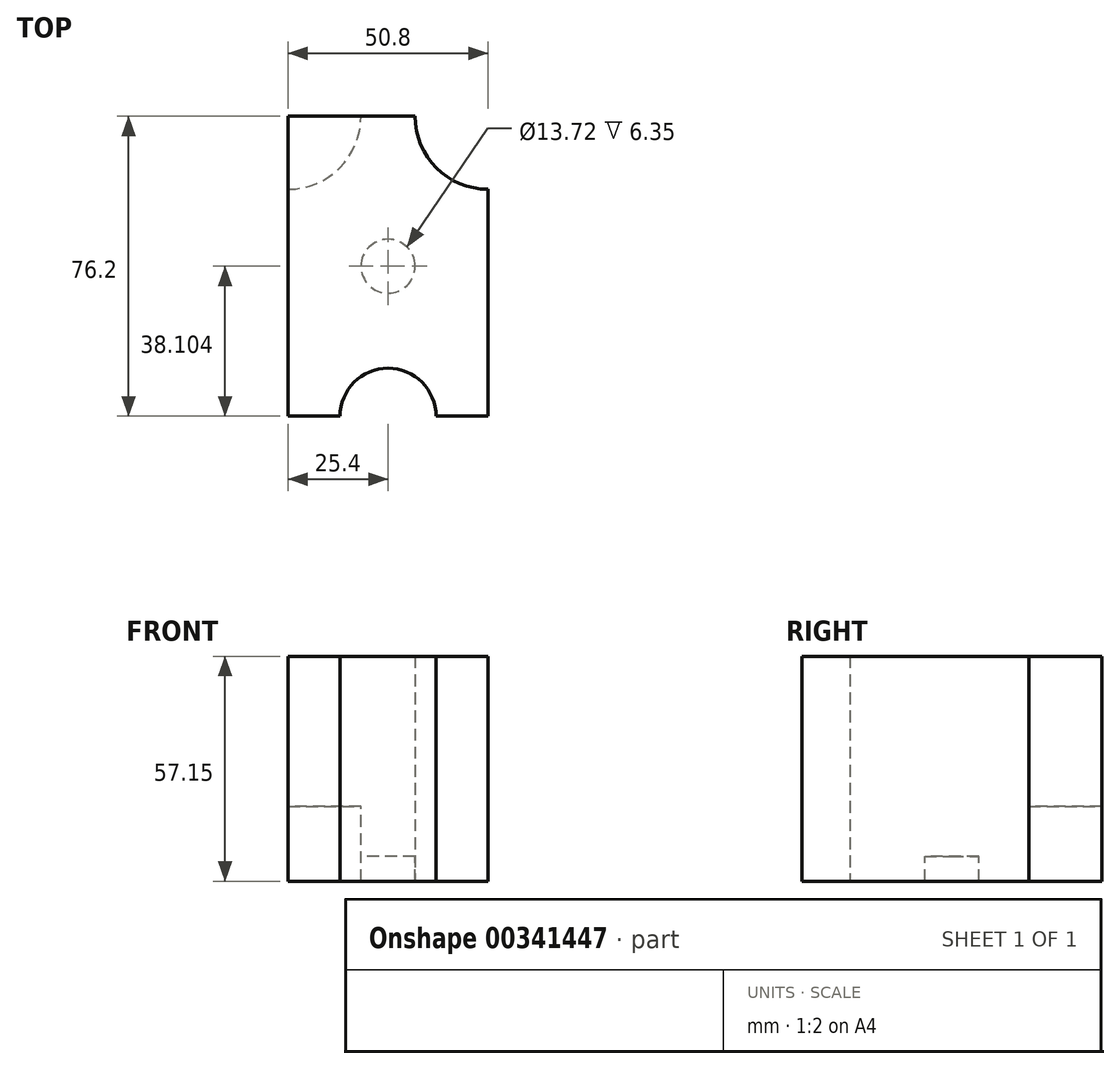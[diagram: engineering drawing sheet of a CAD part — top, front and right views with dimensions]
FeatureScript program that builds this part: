
annotation { "Feature Type Name" : "Feature", "Feature Type Description" : "" }
export const myFeature = defineFeature(function(context is Context, id is Id, definition is map)
    precondition{}
    {
        {
            var Q0;
            Q0=qCreatedBy(makeId("Top.planeOp"),FACE);
            var sketch = newSketch(context, id + "F0", { "sketchPlane" : qUnion([Q0])});
            skLineSegment(sketch, "E0.bottom", {"start": v(25.4, 36.53) * mm, "end": v(-25.4, 36.53) * mm});
            skLineSegment(sketch, "E0.top", {"start": v(25.4, -39.67) * mm, "end": v(-25.4, -39.67) * mm});
            skLineSegment(sketch, "E0.left", {"start": v(25.4, 36.53) * mm, "end": v(25.4, -39.67) * mm});
            skLineSegment(sketch, "E0.right", {"start": v(-25.4, 36.53) * mm, "end": v(-25.4, -39.67) * mm});
            skPoint(sketch, "E0.middle", {"position": v(0, -1.57) * mm});
            skArc(sketch, "E1", {"start": v(-6.86, 36.53) * mm, "mid": v(-12.29, 23.42) * mm, "end": v(-25.4, 18) * mm});
            skArc(sketch, "E2", {"start": v(25.4, 18) * mm, "mid": v(12.29, 23.42) * mm, "end": v(6.86, 36.53) * mm});
            skCircle(sketch, "E3", {"center": v(0, -1.57) * mm, "radius": 6.86 * mm});
            skArc(sketch, "E4", {"start": v(-12.2, -39.67) * mm, "mid": v(0, -27.47) * mm, "end": v(12.2, -39.67) * mm});
            skLineSegment(sketch, "E5.bottom", {"start": v(12.2, 10.63) * mm, "end": v(-12.2, 10.63) * mm});
            skLineSegment(sketch, "E5.top", {"start": v(12.2, -13.76) * mm, "end": v(-12.2, -13.76) * mm});
            skLineSegment(sketch, "E5.left", {"start": v(12.2, 10.63) * mm, "end": v(12.2, -13.76) * mm});
            skLineSegment(sketch, "E5.right", {"start": v(-12.2, 10.63) * mm, "end": v(-12.2, -13.76) * mm});
            skLineSegment(sketch, "E6", {"start": v(-12.2, 10.63) * mm, "end": v(-12.2, 0) * mm});
            skLineSegment(sketch, "E7", {"start": v(12.2, 10.63) * mm, "end": v(12.2, 0) * mm});
            skSolve(sketch);
        }
        {
            var Q0;
            {var subQ3=sQuery(id+"F0.wireOp",EDGE,"E2");Q0=makeQuery(id+"F0.imprint","IMPRINT",FACE,{"disambiguationData":[TD([[makeQuery(id+"F0.imprint","IMPRINT",EDGE,{"derivedFrom":subQ3}),-1.0]])]});}
            var Q1;
            {var subQ2=sQuery(id+"F0.wireOp",EDGE,"E1");Q1=makeQuery(id+"F0.imprint","IMPRINT",FACE,{"disambiguationData":[TD([[makeQuery(id+"F0.imprint","IMPRINT",EDGE,{"derivedFrom":subQ2}),1.0]])]});}
            var Q2;
            {var subQ3=sQuery(id+"F0.wireOp",EDGE,"E1");Q2=makeQuery(id+"F0.imprint","IMPRINT",FACE,{"disambiguationData":[TD([[makeQuery(id+"F0.imprint","IMPRINT",EDGE,{"derivedFrom":subQ3}),-1.0]])]});}
            var Q3;
            Q3=makeQuery(id+"F0.imprint","IMPRINT",FACE,{"disambiguationData":[TD([[makeQuery(id+"F0.imprint","IMPRINT",EDGE,{"derivedFrom":sQuery(id+"F0.wireOp",EDGE,"E3")}),1.0]])]});
            var Q4;
            Q4=makeQuery(id+"F0.imprint","IMPRINT",FACE,{"disambiguationData":[TD([[makeQuery(id+"F0.imprint","IMPRINT",EDGE,{"derivedFrom":sQuery(id+"F0.wireOp",EDGE,"E3")}),-1.0]])]});
            var Q5;
            {var subQ0=sQuery(id+"F0.wireOp",EDGE,"E4");Q5=makeQuery(id+"F0.imprint","IMPRINT",FACE,{"disambiguationData":[TD([[makeQuery(id+"F0.imprint","IMPRINT",EDGE,{"derivedFrom":subQ0}),-1.0]])]});}
            extrude(context, id + "F1", {"entities" : qUnion([Q0, Q1, Q2, Q3, Q4, Q5]), "depth" : 38.1 * mm});
        }
        {
            var Q0;
            {var subQ0=sQuery(id+"F0.wireOp",EDGE,"E4");Q0=makeQuery(id+"F0.imprint","IMPRINT",FACE,{"disambiguationData":[TD([[makeQuery(id+"F0.imprint","IMPRINT",EDGE,{"derivedFrom":subQ0}),-1.0]])]});}
            var Q1;
            Q1=makeQuery(id+"F0.imprint","IMPRINT",FACE,{"disambiguationData":[TD([[makeQuery(id+"F0.imprint","IMPRINT",EDGE,{"derivedFrom":sQuery(id+"F0.wireOp",EDGE,"E3")}),-1.0]])]});
            var Q2;
            {var subQ3=sQuery(id+"F0.wireOp",EDGE,"E2");Q2=makeQuery(id+"F0.imprint","IMPRINT",FACE,{"disambiguationData":[TD([[makeQuery(id+"F0.imprint","IMPRINT",EDGE,{"derivedFrom":subQ3}),-1.0]])]});}
            var Q3;
            {var subQ3=sQuery(id+"F0.wireOp",EDGE,"E1");Q3=makeQuery(id+"F0.imprint","IMPRINT",FACE,{"disambiguationData":[TD([[makeQuery(id+"F0.imprint","IMPRINT",EDGE,{"derivedFrom":subQ3}),-1.0]])]});}
            extrude(context, id + "F2", {"entities" : qUnion([Q0, Q1, Q2, Q3]), "operationType" : NewBodyOperationType.ADD, "oppositeDirection" : true, "depth" : 19.05 * mm});
        }
        {
            var Q0;
            Q0=makeQuery(id+"F0.imprint","IMPRINT",FACE,{"disambiguationData":[TD([[makeQuery(id+"F0.imprint","IMPRINT",EDGE,{"derivedFrom":sQuery(id+"F0.wireOp",EDGE,"E3")}),1.0]])]});
            extrude(context, id + "F3", {"entities" : qUnion([Q0]), "operationType" : NewBodyOperationType.ADD, "oppositeDirection" : true, "depth" : 12.7 * mm});
        }
    });
